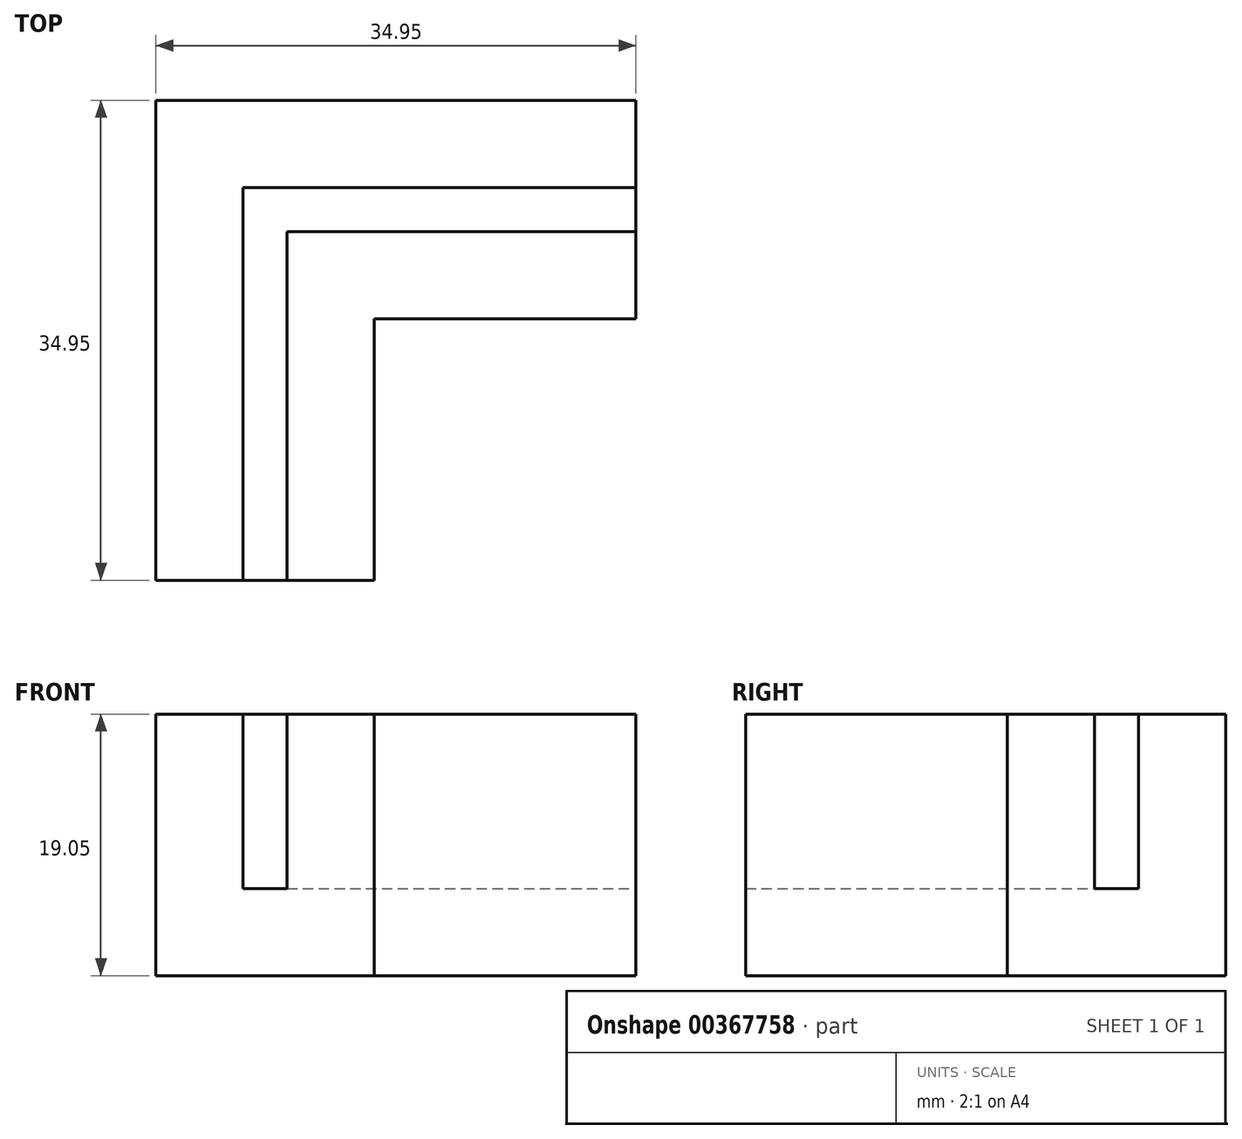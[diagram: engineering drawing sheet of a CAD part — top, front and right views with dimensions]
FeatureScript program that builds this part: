
annotation { "Feature Type Name" : "Feature", "Feature Type Description" : "" }
export const myFeature = defineFeature(function(context is Context, id is Id, definition is map)
    precondition{}
    {
        {
            var Q0;
            Q0=qCreatedBy(makeId("Top.planeOp"),FACE);
            var sketch = newSketch(context, id + "F0", { "sketchPlane" : qUnion([Q0])});
            skLineSegment(sketch, "E0.MirrorCS", {"start": v(27, 1.6) * mm, "end": v(27, 0) * mm});
            skLineSegment(sketch, "E1.MirrorCS", {"start": v(7.95, 7.95) * mm, "end": v(27, 7.95) * mm});
            skLineSegment(sketch, "E2.MirrorCS", {"start": v(1.6, 1.6) * mm, "end": v(27, 1.6) * mm});
            skLineSegment(sketch, "E3.MirrorCS", {"start": v(27, 7.95) * mm, "end": v(27, 1.6) * mm});
            skLineSegment(sketch, "E4.MirrorCS", {"start": v(0, -27) * mm, "end": v(-1.6, -27) * mm});
            skLineSegment(sketch, "E5.MirrorCS", {"start": v(0, -27) * mm, "end": v(1.6, -27) * mm});
            skLineSegment(sketch, "E6.MirrorCS", {"start": v(27, -1.6) * mm, "end": v(27, 0) * mm});
            skLineSegment(sketch, "E7.MirrorCS", {"start": v(-7.95, -27) * mm, "end": v(-7.95, -7.95) * mm});
            skLineSegment(sketch, "E8.MirrorCS", {"start": v(-1.6, -27) * mm, "end": v(-1.6, -1.6) * mm});
            skLineSegment(sketch, "E9.MirrorCS", {"start": v(-7.95, -27) * mm, "end": v(-1.6, -27) * mm});
            skLineSegment(sketch, "E10.MirrorCS", {"start": v(7.95, -7.95) * mm, "end": v(27, -7.95) * mm});
            skLineSegment(sketch, "E11.MirrorCS", {"start": v(7.95, -27) * mm, "end": v(7.95, -7.95) * mm});
            skLineSegment(sketch, "E12.MirrorCS", {"start": v(7.95, -27) * mm, "end": v(1.6, -27) * mm});
            skLineSegment(sketch, "E13.MirrorCS", {"start": v(1.6, -1.6) * mm, "end": v(27, -1.6) * mm});
            skLineSegment(sketch, "E14.MirrorCS", {"start": v(1.6, -27) * mm, "end": v(1.6, -1.6) * mm});
            skLineSegment(sketch, "E15.MirrorCS", {"start": v(27, -7.95) * mm, "end": v(27, -1.6) * mm});
            skLineSegment(sketch, "E16", {"start": v(-7.95, 7.95) * mm, "end": v(-7.95, -7.95) * mm});
            skLineSegment(sketch, "E17", {"start": v(-1.6, 1.6) * mm, "end": v(-1.6, -1.6) * mm});
            skLineSegment(sketch, "E18", {"start": v(7.95, 7.95) * mm, "end": v(-7.95, 7.95) * mm});
            skLineSegment(sketch, "E19", {"start": v(1.6, 1.6) * mm, "end": v(-1.6, 1.6) * mm});
            skSolve(sketch);
        }
        {
            var Q0;
            Q0=makeQuery(id+"F0.imprint","IMPRINT",FACE,{"disambiguationData":[TD([[makeQuery(id+"F0.imprint","IMPRINT",EDGE,{"derivedFrom":sQuery(id+"F0.wireOp",EDGE,"T5vsWyNC-wK1W-Gfbq-GIZy-DRSYmvXTQv4W")}),-1.0]])]});
            var Q1;
            Q1=makeQuery(id+"F0.imprint","IMPRINT",FACE,{"disambiguationData":[TD([[makeQuery(id+"F0.imprint","IMPRINT",EDGE,{"derivedFrom":sQuery(id+"F0.wireOp",EDGE,"E1.MirrorCS")}),-1.0]])]});
            var Q2;
            Q2=makeQuery(id+"F0.imprint","IMPRINT",FACE,{"disambiguationData":[TD([[makeQuery(id+"F0.imprint","IMPRINT",EDGE,{"derivedFrom":sQuery(id+"F0.wireOp",EDGE,"E10.MirrorCS")}),1.0]])]});
            var Q3;
            Q3=makeQuery(id+"F0.imprint","IMPRINT",FACE,{"disambiguationData":[TD([[makeQuery(id+"F0.imprint","IMPRINT",EDGE,{"derivedFrom":sQuery(id+"F0.wireOp",EDGE,"E7.MirrorCS")}),-1.0]])]});
            var Q4;
            Q4=makeQuery(id+"F0.imprint","IMPRINT",FACE,{"disambiguationData":[TD([[makeQuery(id+"F0.imprint","IMPRINT",EDGE,{"derivedFrom":sQuery(id+"F0.wireOp",EDGE,"ZXWAAgie-aylf-geOE-5qcL-ZjX8rLVs7yFz")}),1.0]])]});
            var Q5;
            Q5=makeQuery(id+"F0.imprint","IMPRINT",FACE,{"disambiguationData":[TD([[makeQuery(id+"F0.imprint","IMPRINT",EDGE,{"derivedFrom":sQuery(id+"F0.wireOp",EDGE,"E0.MirrorCS")}),-1.0]])]});
            extrude(context, id + "F1", {"entities" : qUnion([Q0, Q1, Q2, Q3, Q4, Q5]), "oppositeDirection" : true, "depth" : 6.35 * mm});
        }
        {
            var Q0;
            Q0=makeQuery(id+"F0.imprint","IMPRINT",FACE,{"disambiguationData":[TD([[makeQuery(id+"F0.imprint","IMPRINT",EDGE,{"derivedFrom":sQuery(id+"F0.wireOp",EDGE,"T5vsWyNC-wK1W-Gfbq-GIZy-DRSYmvXTQv4W")}),-1.0]])]});
            var Q1;
            Q1=makeQuery(id+"F0.imprint","IMPRINT",FACE,{"disambiguationData":[TD([[makeQuery(id+"F0.imprint","IMPRINT",EDGE,{"derivedFrom":sQuery(id+"F0.wireOp",EDGE,"E1.MirrorCS")}),-1.0]])]});
            var Q2;
            Q2=makeQuery(id+"F0.imprint","IMPRINT",FACE,{"disambiguationData":[TD([[makeQuery(id+"F0.imprint","IMPRINT",EDGE,{"derivedFrom":sQuery(id+"F0.wireOp",EDGE,"E10.MirrorCS")}),1.0]])]});
            var Q3;
            Q3=makeQuery(id+"F0.imprint","IMPRINT",FACE,{"disambiguationData":[TD([[makeQuery(id+"F0.imprint","IMPRINT",EDGE,{"derivedFrom":sQuery(id+"F0.wireOp",EDGE,"E7.MirrorCS")}),-1.0]])]});
            extrude(context, id + "F2", {"entities" : qUnion([Q0, Q1, Q2, Q3]), "operationType" : NewBodyOperationType.ADD, "depth" : 12.7 * mm});
        }
    });
